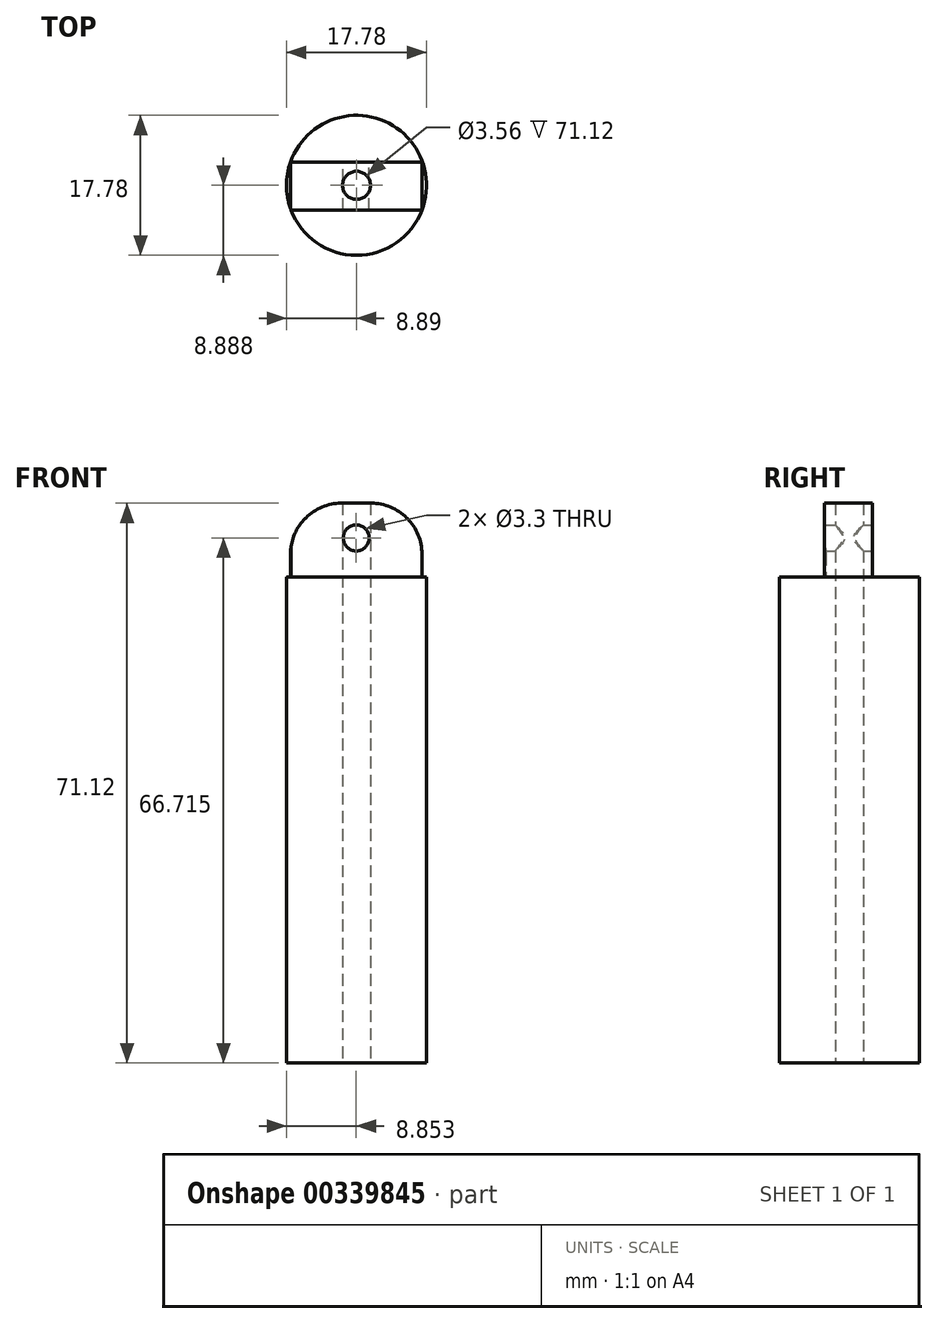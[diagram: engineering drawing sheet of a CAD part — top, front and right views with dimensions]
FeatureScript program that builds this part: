
annotation { "Feature Type Name" : "Feature", "Feature Type Description" : "" }
export const myFeature = defineFeature(function(context is Context, id is Id, definition is map)
    precondition{}
    {
        {
            var Q0;
            Q0=qCreatedBy(makeId("Top.planeOp"),FACE);
            var sketch = newSketch(context, id + "F0", { "sketchPlane" : qUnion([Q0])});
            skCircle(sketch, "E0", {"center": v(-23.34, 17.46) * mm, "radius": 8.89 * mm});
            skCircle(sketch, "E1", {"center": v(-23.34, 17.46) * mm, "radius": 1.78 * mm});
            skSolve(sketch);
        }
        {
            var Q0;
            Q0=makeQuery(id+"F0.imprint","IMPRINT",FACE,{"disambiguationData":[TD([[makeQuery(id+"F0.imprint","IMPRINT",EDGE,{"derivedFrom":sQuery(id+"F0.wireOp",EDGE,"E0")}),1.0]])]});
            extrude(context, id + "F1", {"entities" : qUnion([Q0]), "depth" : 61.72 * mm});
        }
        {
            var Q0;
            Q0=makeQuery(id+"F1.opExtrude","CAP_FACE",FACE,{"disambiguationData":[OSD([sQuery(id+"F0.wireOp",EDGE,"E0"),sQuery(id+"F0.wireOp",EDGE,"E1")])],"isStart":false});
            var sketch = newSketch(context, id + "F2", { "sketchPlane" : qUnion([Q0])});
            skLineSegment(sketch, "E2.bottom", {"start": v(-31.73, 20.4) * mm, "end": v(-15.02, 20.4) * mm});
            skLineSegment(sketch, "E2.top", {"start": v(-31.73, 14.32) * mm, "end": v(-15.02, 14.32) * mm});
            skLineSegment(sketch, "E2.left", {"start": v(-31.73, 20.4) * mm, "end": v(-31.73, 14.32) * mm});
            skLineSegment(sketch, "E2.right", {"start": v(-15.02, 20.4) * mm, "end": v(-15.02, 14.32) * mm});
            skSolve(sketch);
        }
        {
            var Q0;
            {var subQ1=sQuery(id+"F2.wireOp",EDGE,"E2.bottom");Q0=makeQuery(id+"F2.imprint","IMPRINT",FACE,{"disambiguationData":[TD([[makeQuery(id+"F2.imprint","IMPRINT",EDGE,{"derivedFrom":subQ1}),-1.0]])]});}
            extrude(context, id + "F3", {"entities" : qUnion([Q0]), "operationType" : NewBodyOperationType.ADD, "depth" : 9.4 * mm});
        }
        {
            var Q0;
            Q0=makeQuery(id+"F3.opExtrude","CAP_EDGE",EDGE,{"disambiguationData":[OSD([sQuery(id+"F2.wireOp",EDGE,"E2.right")])],"isStart":false});
            var Q1;
            Q1=makeQuery(id+"F3.opExtrude","CAP_EDGE",EDGE,{"disambiguationData":[OSD([sQuery(id+"F2.wireOp",EDGE,"E2.left")])],"isStart":false});
            chamfer(context, id + "F4", {"entities" : qUnion([Q0, Q1]), "width" : 3.8 * mm, "tangentPropagation" : true});
        }
        {
            var Q0;
            {var subQ0=sQuery(id+"F2.wireOp",EDGE,"E2.left");Q0=makeQuery(id+"F4.opChamfer","BLEND_EDGE",EDGE,{"blendedFrom":[makeQuery(id+"F3.opExtrude","CAP_EDGE",EDGE,{"disambiguationData":[OSD([subQ0])],"isStart":false}),makeQuery(id+"F3.opExtrude","CAP_FACE",FACE,{"disambiguationData":[OSD([sQuery(id+"F0.wireOp",EDGE,"E0"),sQuery(id+"F0.wireOp",EDGE,"E1"),sQuery(id+"F2.wireOp",EDGE,"E2.bottom"),sQuery(id+"F2.wireOp",EDGE,"E2.top"),subQ0,sQuery(id+"F2.wireOp",EDGE,"E2.right")])],"isStart":false})],"blendedInto":[makeQuery(id+"F3.opExtrude","CAP_FACE",FACE,{"disambiguationData":[OSD([sQuery(id+"F0.wireOp",EDGE,"E0"),sQuery(id+"F0.wireOp",EDGE,"E1"),sQuery(id+"F2.wireOp",EDGE,"E2.bottom"),sQuery(id+"F2.wireOp",EDGE,"E2.top"),subQ0,sQuery(id+"F2.wireOp",EDGE,"E2.right")])],"isStart":false})]});}
            var Q1;
            {var subQ0=sQuery(id+"F2.wireOp",EDGE,"E2.right");Q1=makeQuery(id+"F4.opChamfer","BLEND_EDGE",EDGE,{"blendedFrom":[makeQuery(id+"F3.opExtrude","CAP_EDGE",EDGE,{"disambiguationData":[OSD([subQ0])],"isStart":false}),makeQuery(id+"F3.opExtrude","CAP_FACE",FACE,{"disambiguationData":[OSD([sQuery(id+"F0.wireOp",EDGE,"E0"),sQuery(id+"F0.wireOp",EDGE,"E1"),sQuery(id+"F2.wireOp",EDGE,"E2.bottom"),sQuery(id+"F2.wireOp",EDGE,"E2.top"),sQuery(id+"F2.wireOp",EDGE,"E2.left"),subQ0])],"isStart":false})],"blendedInto":[makeQuery(id+"F3.opExtrude","CAP_FACE",FACE,{"disambiguationData":[OSD([sQuery(id+"F0.wireOp",EDGE,"E0"),sQuery(id+"F0.wireOp",EDGE,"E1"),sQuery(id+"F2.wireOp",EDGE,"E2.bottom"),sQuery(id+"F2.wireOp",EDGE,"E2.top"),sQuery(id+"F2.wireOp",EDGE,"E2.left"),subQ0])],"isStart":false})]});}
            var Q2;
            {var subQ0=sQuery(id+"F2.wireOp",EDGE,"E2.right");Q2=makeQuery(id+"F4.opChamfer","BLEND_EDGE",EDGE,{"blendedFrom":[makeQuery(id+"F3.opExtrude","CAP_EDGE",EDGE,{"disambiguationData":[OSD([subQ0])],"isStart":false}),makeQuery(id+"F3.opExtrude","SWEPT_FACE",FACE,{"disambiguationData":[OSD([subQ0])]})],"blendedInto":[makeQuery(id+"F3.opExtrude","SWEPT_FACE",FACE,{"disambiguationData":[OSD([subQ0])]})]});}
            var Q3;
            {var subQ0=sQuery(id+"F2.wireOp",EDGE,"E2.left");Q3=makeQuery(id+"F4.opChamfer","BLEND_EDGE",EDGE,{"blendedFrom":[makeQuery(id+"F3.opExtrude","CAP_EDGE",EDGE,{"disambiguationData":[OSD([subQ0])],"isStart":false}),makeQuery(id+"F3.opExtrude","SWEPT_FACE",FACE,{"disambiguationData":[OSD([subQ0])]})],"blendedInto":[makeQuery(id+"F3.opExtrude","SWEPT_FACE",FACE,{"disambiguationData":[OSD([subQ0])]})]});}
            fillet(context, id + "F5", {"entities" : qUnion([Q0, Q1, Q2, Q3]), "radius" : 6.35 * mm, "tangentPropagation" : true, "allowEdgeOverflow" : false});
        }
        {
            var Q0;
            Q0=makeQuery(id+"F3.opExtrude","SWEPT_FACE",FACE,{"disambiguationData":[OSD([sQuery(id+"F2.wireOp",EDGE,"E2.top")])]});
            var sketch = newSketch(context, id + "F6", { "sketchPlane" : qUnion([Q0])});
            skCircle(sketch, "E3", {"center": v(-23.38, 66.71) * mm, "radius": 3.18 * mm});
            skPoint(sketch, "E3.centerSnap0", {"position": v(-23.38, 71.12) * mm});
            skSolve(sketch);
        }
        {
            var Q0;
            Q0=sQuery(id+"F6.wireOp",VERTEX,"E3.center");
            var Q1;
            Q1=makeQuery(id+"F1.opExtrude","SWEPT_BODY",BODY,{"disambiguationData":[OSD([sQuery(id+"F0.wireOp",EDGE,"E0"),sQuery(id+"F0.wireOp",EDGE,"E1")])]});
            hole(context, id + "F7", {"style" : HoleStyle.SIMPLE, "endStyle" : HoleEndStyle.THROUGH, "standardTappedOrClearance" : lookupTablePath({ "standard" : "ISO", "fit" : "Normal", "size" : "M3", "type" : "Clearance" }), "standardBlindInLast" : lookupTablePath({ "fit" : "Standard", "standard" : "ISO", "size" : "M3", "type" : "Clearance" }), "holeDiameter" : 3.3 * mm, "isTappedThrough" : true, "tappedDepth" : 12.7 * mm, "tapClearance" : 3, "locations" : qUnion([Q0]), "scope" : qUnion([Q1]), "startStyle" : HoleStartStyle.PART});
        }
    });
